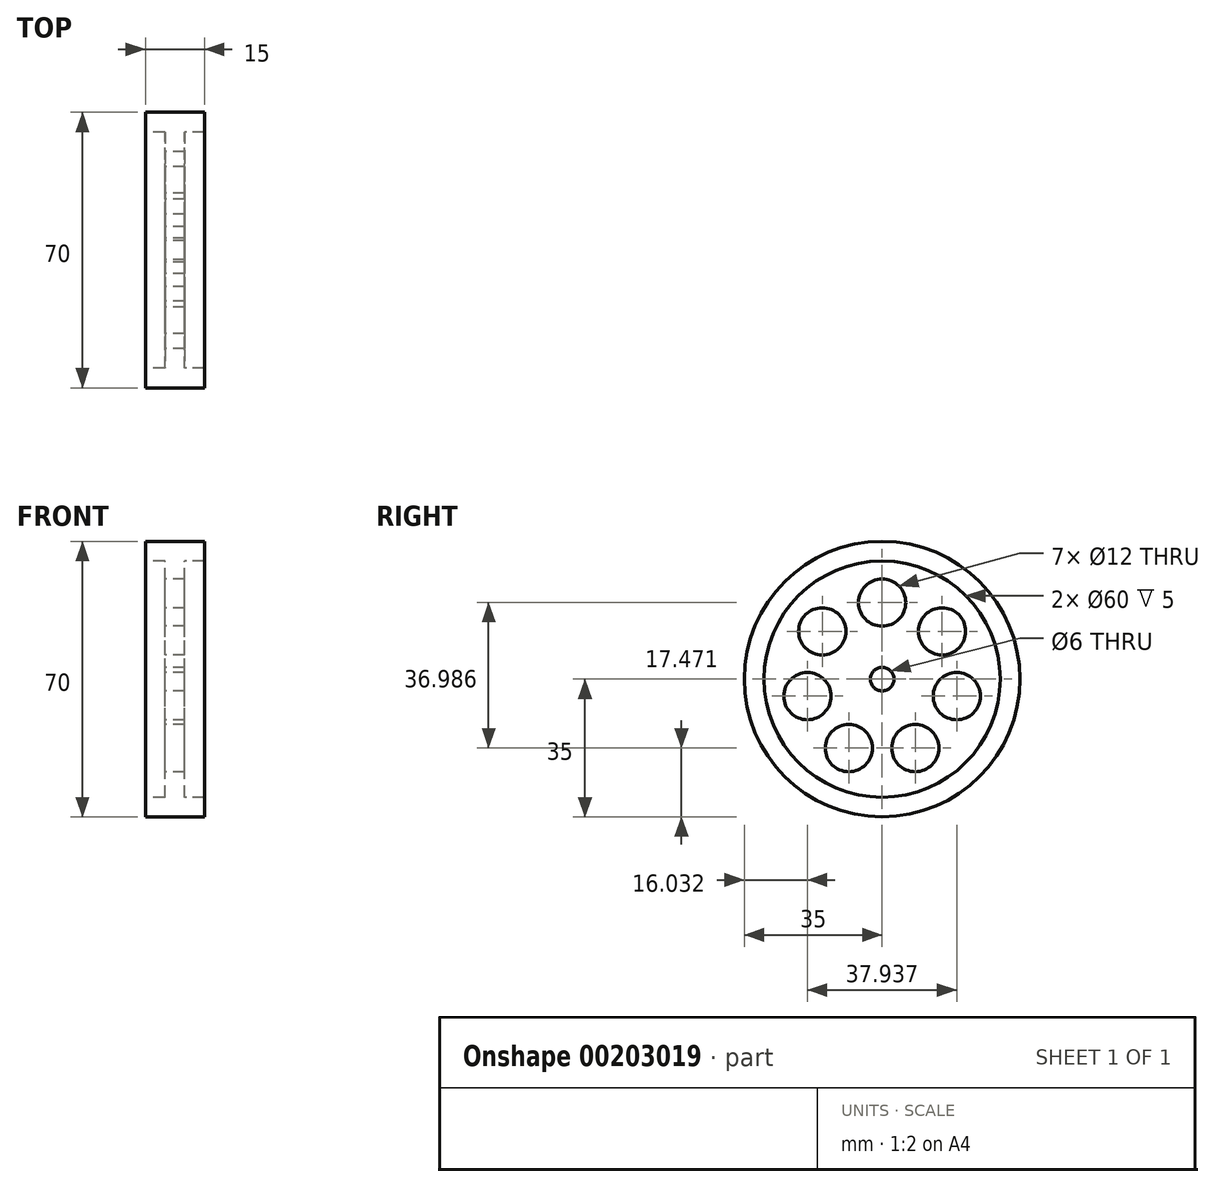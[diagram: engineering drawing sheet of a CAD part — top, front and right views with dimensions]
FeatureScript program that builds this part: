
annotation { "Feature Type Name" : "Feature", "Feature Type Description" : "" }
export const myFeature = defineFeature(function(context is Context, id is Id, definition is map)
    precondition{}
    {
        {
            var Q0;
            Q0=qCreatedBy(makeId("Right.planeOp"),FACE);
            var sketch = newSketch(context, id + "F0", { "sketchPlane" : qUnion([Q0])});
            skCircle(sketch, "E0", {"center": v(0, 0) * mm, "radius": 35 * mm});
            skCircle(sketch, "E1", {"center": v(0, 0) * mm, "radius": 3 * mm});
            skCircle(sketch, "E2", {"center": v(0, 19.46) * mm, "radius": 6 * mm});
            skCircle(sketch, "E3.1.0", {"center": v(-15.21, 12.13) * mm, "radius": 6 * mm});
            skCircle(sketch, "E3.2.0", {"center": v(-18.97, -4.33) * mm, "radius": 6 * mm});
            skCircle(sketch, "E4.1.3.0", {"center": v(-8.44, -17.53) * mm, "radius": 6 * mm});
            skCircle(sketch, "E5.1.4.0", {"center": v(8.44, -17.53) * mm, "radius": 6 * mm});
            skCircle(sketch, "E6.1.5.0", {"center": v(18.97, -4.33) * mm, "radius": 6 * mm});
            skCircle(sketch, "E6.1.6.0", {"center": v(15.21, 12.13) * mm, "radius": 6 * mm});
            skSolve(sketch);
        }
        {
            var Q0;
            Q0=makeQuery(id+"F0.imprint","IMPRINT",FACE,{"disambiguationData":[TD([[makeQuery(id+"F0.imprint","IMPRINT",EDGE,{"derivedFrom":sQuery(id+"F0.wireOp",EDGE,"E0")}),1.0]])]});
            extrude(context, id + "F1", {"entities" : qUnion([Q0]), "depth" : 5 * mm});
        }
        {
            var Q0;
            Q0=qCreatedBy(makeId("Right.planeOp"),FACE);
            var sketch = newSketch(context, id + "F2", { "sketchPlane" : qUnion([Q0])});
            skCircle(sketch, "E7", {"center": v(0, 0) * mm, "radius": 30 * mm});
            skCircle(sketch, "E8.0", {"center": v(0, 0) * mm, "radius": 35 * mm});
            skSolve(sketch);
        }
        {
            var Q0;
            Q0=makeQuery(id+"F2.imprint","IMPRINT",FACE,{"disambiguationData":[TD([[makeQuery(id+"F2.imprint","IMPRINT",EDGE,{"derivedFrom":sQuery(id+"F2.wireOp",EDGE,"E7")}),-1.0]])]});
            extrude(context, id + "F3", {"entities" : qUnion([Q0]), "operationType" : NewBodyOperationType.ADD, "depth" : 10 * mm, "hasSecondDirection" : true, "secondDirectionOppositeDirection" : true, "secondDirectionDepth" : 5 * mm});
        }
    });
